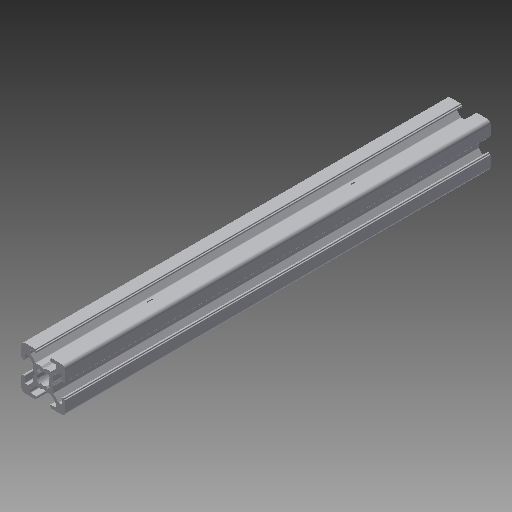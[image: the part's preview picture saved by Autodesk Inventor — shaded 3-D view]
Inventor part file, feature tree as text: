
AUTODESK INVENTOR PART (.ipt)
format: ipt  version: 2017 (Build 210142000, 142)  size: 409,088 bytes
history: native  units: in
note: dims shown in document units (in); Inventor stores cm internally (conversion verified against a paired STEP export)
features: other x3, sketch x2, extrude x1, hole x1, mirror x1
ambient origin geometry x8: Origin, YZ Plane, XZ Plane, XY Plane, X Axis, Y Axis, Z Axis, Center Point
bodies: Solid1 (feature_tree)
feature tree (8):
  other  "Blocks"
  extrude  "Extrusion1"  Depth=2.0in
  hole  "Hole1"  [1 undecoded]
  mirror  "Mirror1"
  sketch  "Sketch1"  dims[d1=0.0in d5=2.0in]
  other  "20x20"
  sketch  "Sketch3"  dims[d6=0.187in d7=0.75in d8=0.375in d9=0.25in d10=0.5635in d11=1.0in d12=0.8108in d13=1.0in d14=1.0in]
  other  "20x20:1"
note: 1 required parameter value undecoded (feature->parameter linkage not recoverable at this tier; creation-order binding heuristic only, values carry confidence <= 0.55)
